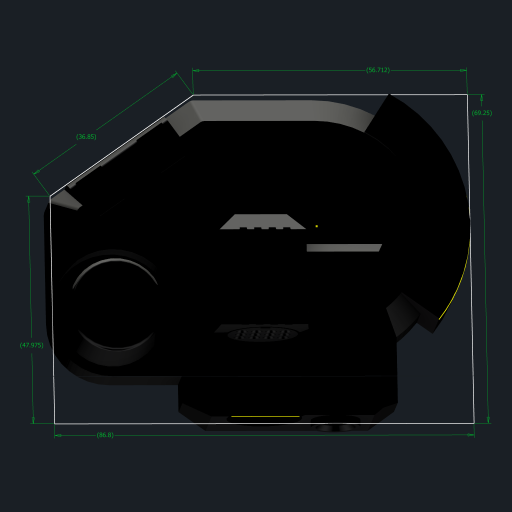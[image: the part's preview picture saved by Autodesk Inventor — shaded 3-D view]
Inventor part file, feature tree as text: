
AUTODESK INVENTOR PART (.ipt)
format: ipt  version: 2023 (Build 270158000, 158)  size: 608,768 bytes
history: native  units: in
note: dims shown in document units (in); Inventor stores cm internally (conversion verified against a paired STEP export)
features: sketch x21, extrude x20, chamfer x6, projected_geometry x6, fillet x5, boolean_combine x1, direct_edit x1, other x1
ambient origin geometry x8: Origin, YZ Plane, XZ Plane, XY Plane, X Axis, Y Axis, Z Axis, Center Point
bodies: Solid1 (feature_tree), Solid2 (feature_tree)
feature tree (61):
  extrude  "Extrusion1"  Depth=2.6673in
  extrude  "Extrusion2"  Depth=0.0787in
  extrude  "Extrusion3"  Depth=1.7559in
  extrude  "Extrusion4"  Depth=0.9449in
  fillet  "Fillet1"  Radius=1.4508in
  fillet  "Fillet2"  Radius=0.9449in
  fillet  "Fillet4"  Radius=0.9843in
  sketch  "Sketch7"  dims[d12=0.5441in d13=0.3543in d14=0.0in]
  sketch  "Sketch8"  dims[d15=0.2165in d16=-0.3092in d18=0.8508in]
  extrude  "Extrusion5"  Depth=0.3543in TaperAngle=0.0deg
  extrude  "Extrusion6"  Depth=0.8508in
  extrude  "Extrusion7"  Depth=0.8508in
  extrude  "Extrusion8"  Depth=0.0787in
  extrude  "Extrusion9"  Depth=0.0394in
  chamfer  "Chamfer1"  Distance=1.4173in
  chamfer  "Chamfer2"  Distance=1.4173in
  chamfer  "Chamfer3"  Distance=0.6957in
  boolean_combine  "Combine1"
  extrude  "Extrusion10"  Depth=0.8996in
  extrude  "Extrusion11"  Depth=0.7874in TaperAngle=0.0deg
  extrude  "Extrusion12"  Depth=0.1575in TaperAngle=45.0deg
  extrude  "Extrusion13"  Depth=0.0787in TaperAngle=45.0deg
  chamfer  "Chamfer4"  Distance=0.2362in
  chamfer  "Chamfer5"  Distance=0.2362in
  extrude  "Extrusion14"  Depth=0.0394in
  extrude  "Extrusion15"  Depth=0.3543in
  chamfer  "Chamfer6"  Distance=0.2362in
  extrude  "Extrusion16"  Depth=0.0591in
  extrude  "Extrusion17"  Depth=0.1181in
  extrude  "Extrusion18"  Depth=0.1181in
  fillet  "Fillet6"  Radius=0.2362in
  extrude  "Extrusion19"  Depth=0.0197in TaperAngle=45.0deg
  extrude  "Extrusion20"  Depth=0.0787in TaperAngle=45.0deg
  direct_edit  "Direct Edit1"
  fillet  "Fillet7"  Radius=0.4043in
  sketch  "Sketch24"  dims[d64=0.2362in d65=0.0in d66=0.3543in d69=0.2362in d70=0.0591in d71=0.1181in d72=0.1181in d73=0.2362in d74=0.0in d75=0.0197in d76=0.125in d77=45.0deg d78=0.0787in d79=0.125in d80=45.0deg d81=0.4043in d82=0.3006in d83=0.0591in d84=0.0in d86=0.252in d87=0.3937in d88=0.0in d89=0.0394in d90=0.125in d91=45.0deg d92=0.1575in d93=0.6102in d94=0.0in d95=0.6102in d96=0.0in d98=0.9843in d99=1.0in d100=0.0in d101=0.0591in d102=0.0394in d103=0.3327in d104=0.0591in d105=0.25in d106=0.0394in d107=0.0in d108=0.0197in d109=0.0in d110=0.0049in d111=1.4508in d112=2.2327in d113=1.8888in d114=3.4173in d115=2.7264in d56=0.0in]
  sketch  "Sketch1"  dims[d0=3.2598in d1=2.6673in]
  sketch  "Sketch2"  dims[d2=0.8508in d3=0.0787in]
  projected_geometry  "Projected Loop1"
  sketch  "Sketch4"  dims[d4=1.7559in d5=0.1575in]
  sketch  "Sketch5"  dims[d6=0.2165in d7=0.439in d9=1.4508in d10=0.9449in d11=0.9843in]
  projected_geometry  "Projected Loop2"
  sketch  "Sketch9"  dims[d19=0.2165in d20=0.0in d21=0.8508in]
  sketch  "Sketch10"  dims[d22=0.4488in d23=-0.0344in d24=0.0787in]
  sketch  "Sketch11"  dims[d25=0.0787in d27=0.0394in]
  projected_geometry  "Projected Loop3"
  sketch  "Sketch12"  dims[d28=0.702in]
  sketch  "Sketch13"  dims[d29=0.5846in]
  projected_geometry  "Projected Loop4"
  sketch  "Sketch14"  dims[d31=0.7902in]
  projected_geometry  "Projected Loop5"
  sketch  "Sketch15"  dims[d32=0.7902in]
  sketch  "Sketch17"  dims[d33=0.6142in d34=1.4173in d35=0.0in d36=1.4173in d37=0.0in d38=0.6957in d39=0.0in]
  sketch  "Sketch18"  dims[d40=0.8996in d41=0.6597in]
  projected_geometry  "Projected Loop6"
  sketch  "Sketch19"  dims[d42=0.6597in d43=0.7874in d44=0.0in]
  sketch  "Sketch20"  dims[d45=0.1575in d46=0.0in d47=0.1575in d48=0.125in d49=45.0deg]
  sketch  "Sketch21"  dims[d50=0.1575in d51=0.125in d52=45.0deg d53=0.0787in d54=0.125in d55=45.0deg d57=0.2362in d58=0.0in]
  sketch  "Sketch22"  dims[d59=0.0197in d60=0.2362in d61=0.0in]
  sketch  "Sketch23"  dims[d62=0.0787in d63=0.0394in]
  other  "Delete1"
